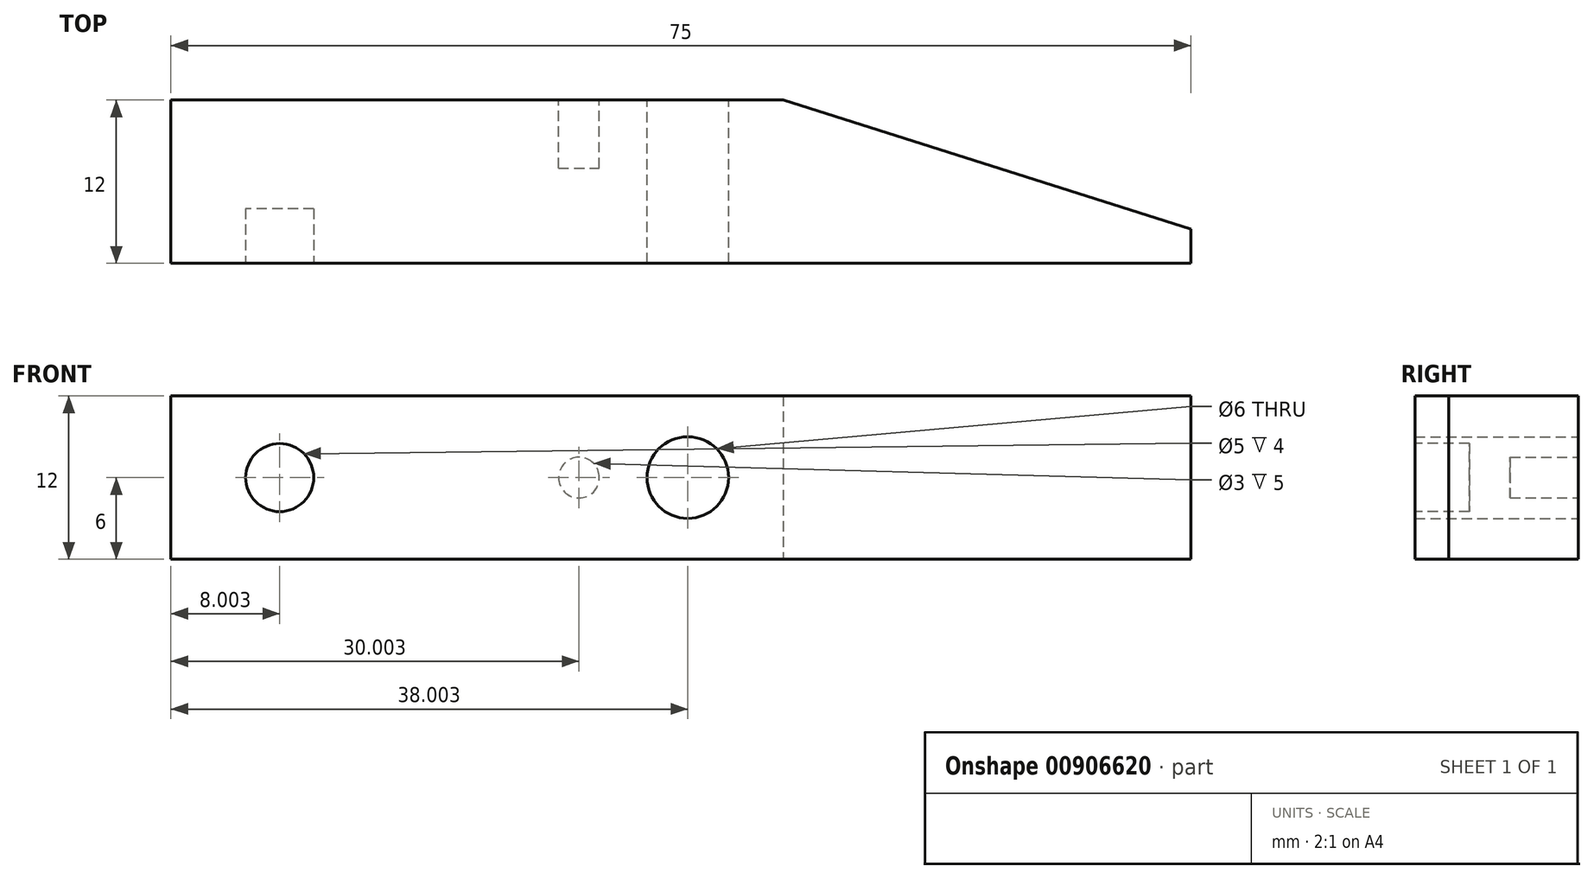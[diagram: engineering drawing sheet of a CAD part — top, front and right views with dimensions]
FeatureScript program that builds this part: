
annotation { "Feature Type Name" : "Feature", "Feature Type Description" : "" }
export const myFeature = defineFeature(function(context is Context, id is Id, definition is map)
    precondition{}
    {
        {
            var Q0;
            Q0=qCreatedBy(makeId("Top.planeOp"),FACE);
            var sketch = newSketch(context, id + "F0", { "sketchPlane" : qUnion([Q0])});
            skLineSegment(sketch, "E0", {"start": v(-19.32, 22.42) * mm, "end": v(25.68, 22.42) * mm});
            skLineSegment(sketch, "E1", {"start": v(25.68, 22.42) * mm, "end": v(55.68, 12.92) * mm});
            skLineSegment(sketch, "E2", {"start": v(55.68, 12.92) * mm, "end": v(55.68, 10.42) * mm});
            skLineSegment(sketch, "E3", {"start": v(55.68, 10.42) * mm, "end": v(-19.32, 10.42) * mm});
            skLineSegment(sketch, "E4", {"start": v(-19.32, 10.42) * mm, "end": v(-19.32, 22.42) * mm});
            skSolve(sketch);
        }
        {
            var Q0;
            Q0=makeQuery(id+"F0.imprint","IMPRINT",FACE,{"disambiguationData":[TD([[makeQuery(id+"F0.imprint","IMPRINT",EDGE,{"derivedFrom":sQuery(id+"F0.wireOp",EDGE,"E0")}),-1.0]])]});
            extrude(context, id + "F1", {"entities" : qUnion([Q0]), "depth" : 12 * mm, "offsetDistance" : 25 * mm});
        }
        {
            var Q0;
            Q0=makeQuery(id+"F1.opExtrude","SWEPT_FACE",FACE,{"disambiguationData":[OSD([sQuery(id+"F0.wireOp",EDGE,"E0")])]});
            var sketch = newSketch(context, id + "F2", { "sketchPlane" : qUnion([Q0])});
            skPoint(sketch, "E5", {"position": v(-18.68, 6) * mm});
            skPoint(sketch, "E6", {"position": v(11.32, 6) * mm});
            skCircle(sketch, "E7", {"center": v(-18.68, 6) * mm, "radius": 3 * mm});
            skSolve(sketch);
        }
        {
            var Q0;
            Q0 = qSketchRegion(id + "F2", true);
            extrude(context, id + "F3", {"entities" : qUnion([Q0]), "operationType" : NewBodyOperationType.REMOVE, "endBound" : BoundingType.THROUGH_ALL, "oppositeDirection" : true, "depth" : 25 * mm, "offsetDistance" : 25 * mm});
        }
        {
            var Q0;
            Q0=makeQuery(id+"F1.opExtrude","SWEPT_FACE",FACE,{"disambiguationData":[OSD([sQuery(id+"F0.wireOp",EDGE,"E3")])]});
            var sketch = newSketch(context, id + "F4", { "sketchPlane" : qUnion([Q0])});
            skPoint(sketch, "E8", {"position": v(-11.32, 6) * mm});
            skCircle(sketch, "E9", {"center": v(-11.32, 6) * mm, "radius": 2.5 * mm});
            skSolve(sketch);
        }
        {
            var Q0;
            Q0=makeQuery(id+"F4.imprint","IMPRINT",FACE,{"disambiguationData":[TD([[makeQuery(id+"F4.imprint","IMPRINT",EDGE,{"derivedFrom":sQuery(id+"F4.wireOp",EDGE,"E9")}),1.0]])]});
            extrude(context, id + "F5", {"entities" : qUnion([Q0]), "operationType" : NewBodyOperationType.REMOVE, "oppositeDirection" : true, "depth" : 4 * mm, "offsetDistance" : 25 * mm});
        }
        {
            var Q0;
            Q0=makeQuery(id+"F1.opExtrude","SWEPT_FACE",FACE,{"disambiguationData":[OSD([sQuery(id+"F0.wireOp",EDGE,"E0")])]});
            var sketch = newSketch(context, id + "F6", { "sketchPlane" : qUnion([Q0])});
            skPoint(sketch, "E10", {"position": v(-10.68, 6) * mm});
            skPoint(sketch, "E11", {"position": v(-18.68, 6) * mm});
            skCircle(sketch, "E12", {"center": v(-10.68, 6) * mm, "radius": 1.5 * mm});
            skSolve(sketch);
        }
        {
            var Q0;
            Q0=makeQuery(id+"F6.imprint","IMPRINT",FACE,{"disambiguationData":[TD([[makeQuery(id+"F6.imprint","IMPRINT",EDGE,{"derivedFrom":sQuery(id+"F6.wireOp",EDGE,"E12")}),1.0]])]});
            extrude(context, id + "F7", {"entities" : qUnion([Q0]), "operationType" : NewBodyOperationType.REMOVE, "oppositeDirection" : true, "depth" : 5 * mm, "offsetDistance" : 25 * mm});
        }
    });
